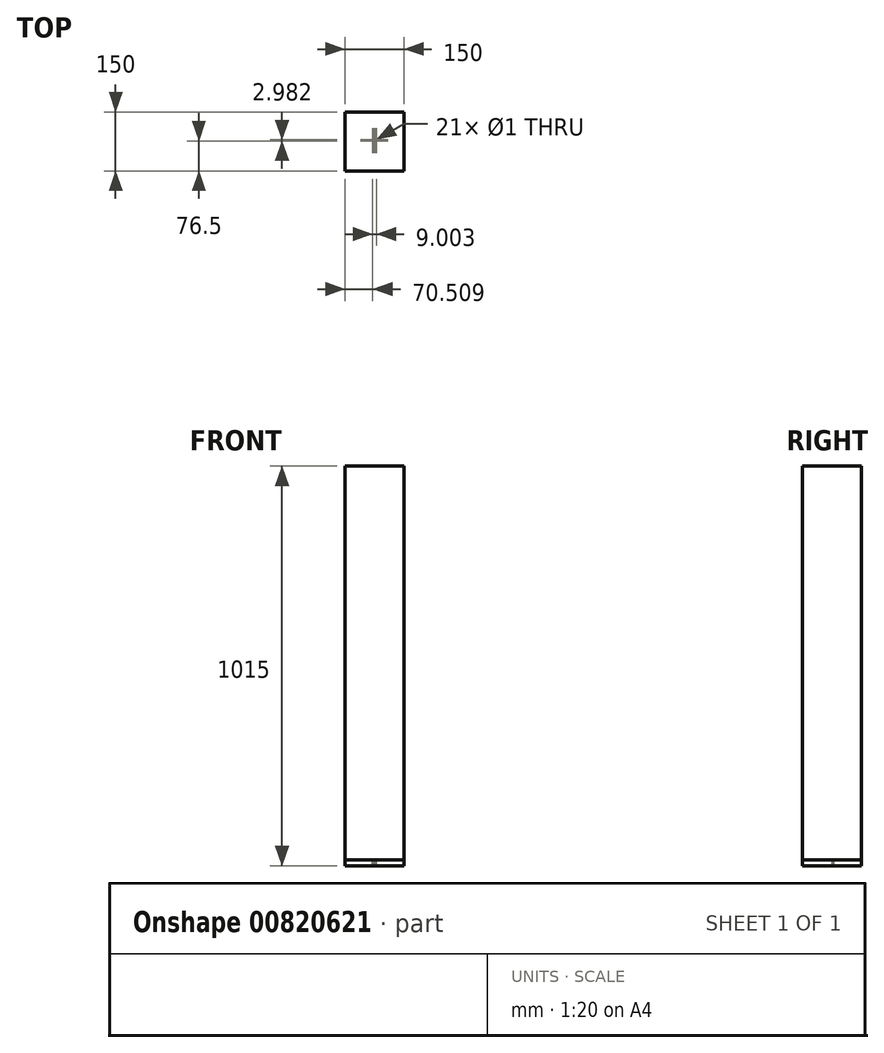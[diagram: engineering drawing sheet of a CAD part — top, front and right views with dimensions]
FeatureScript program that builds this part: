
annotation { "Feature Type Name" : "Feature", "Feature Type Description" : "" }
export const myFeature = defineFeature(function(context is Context, id is Id, definition is map)
    precondition{}
    {
        {
            var Q0;
            Q0=qCreatedBy(makeId("Top.planeOp"),FACE);
            var sketch = newSketch(context, id + "F0", { "sketchPlane" : qUnion([Q0])});
            skLineSegment(sketch, "E0.bottom", {"start": v(75, -75) * mm, "end": v(-75, -75) * mm});
            skLineSegment(sketch, "E0.top", {"start": v(75, 75) * mm, "end": v(-75, 75) * mm});
            skLineSegment(sketch, "E0.left", {"start": v(75, -75) * mm, "end": v(75, 75) * mm});
            skLineSegment(sketch, "E0.right", {"start": v(-75, -75) * mm, "end": v(-75, 75) * mm});
            skPoint(sketch, "E0.middle", {"position": v(0, 0) * mm});
            skSolve(sketch);
        }
        {
            var Q0;
            Q0=makeQuery(id+"F0.imprint","IMPRINT",FACE,{"disambiguationData":[TD([[makeQuery(id+"F0.imprint","IMPRINT",EDGE,{"derivedFrom":sQuery(id+"F0.wireOp",EDGE,"E0.bottom")}),-1.0]])]});
            extrude(context, id + "F1", {"entities" : qUnion([Q0]), "depth" : 1000 * mm, "offsetDistance" : 25 * mm});
        }
        {
            var Q0;
            Q0=makeQuery(id+"F1.opExtrude","CAP_FACE",FACE,{"disambiguationData":[OSD([sQuery(id+"F0.wireOp",EDGE,"E0.bottom"),sQuery(id+"F0.wireOp",EDGE,"E0.top"),sQuery(id+"F0.wireOp",EDGE,"E0.left"),sQuery(id+"F0.wireOp",EDGE,"E0.right")])],"isStart":true});
            var sketch = newSketch(context, id + "F2", { "sketchPlane" : qUnion([Q0])});
            skCircle(sketch, "E1", {"center": v(0, 0) * mm, "radius": 0.5 * mm});
            skCircle(sketch, "E2.1.0.0", {"center": v(1.5, 0) * mm, "radius": 0.5 * mm});
            skCircle(sketch, "E3.0.2.0", {"center": v(3, 0) * mm, "radius": 0.5 * mm});
            skCircle(sketch, "E4.0.3.0", {"center": v(4.5, 0) * mm, "radius": 0.5 * mm});
            skCircle(sketch, "E5.1.0.0", {"center": v(-1.5, 0) * mm, "radius": 0.5 * mm});
            skCircle(sketch, "E5.2.0.0", {"center": v(-3, 0) * mm, "radius": 0.5 * mm});
            skCircle(sketch, "E5.3.0.0", {"center": v(-4.5, 0) * mm, "radius": 0.5 * mm});
            skCircle(sketch, "E6", {"center": v(0.01, 1.5) * mm, "radius": 0.5 * mm});
            skCircle(sketch, "E7.1.0.0", {"center": v(1.51, 1.5) * mm, "radius": 0.5 * mm});
            skCircle(sketch, "E7.2.0.0", {"center": v(3.01, 1.5) * mm, "radius": 0.5 * mm});
            skCircle(sketch, "E7.3.0.0", {"center": v(4.51, 1.5) * mm, "radius": 0.5 * mm});
            skCircle(sketch, "E8.1.0.0", {"center": v(-1.49, 1.5) * mm, "radius": 0.5 * mm});
            skCircle(sketch, "E8.2.0.0", {"center": v(-2.99, 1.5) * mm, "radius": 0.5 * mm});
            skCircle(sketch, "E8.3.0.0", {"center": v(-4.49, 1.5) * mm, "radius": 0.5 * mm});
            skCircle(sketch, "E9", {"center": v(0, 3) * mm, "radius": 0.5 * mm});
            skCircle(sketch, "E10", {"center": v(0, 4.48) * mm, "radius": 0.5 * mm});
            skCircle(sketch, "E11.1.0.0", {"center": v(1.5, 3) * mm, "radius": 0.5 * mm});
            skCircle(sketch, "E11.1.0.1", {"center": v(1.5, 4.48) * mm, "radius": 0.5 * mm});
            skCircle(sketch, "E11.2.0.0", {"center": v(3, 3) * mm, "radius": 0.5 * mm});
            skCircle(sketch, "E11.2.0.1", {"center": v(3, 4.48) * mm, "radius": 0.5 * mm});
            skCircle(sketch, "E11.3.0.0", {"center": v(4.5, 3) * mm, "radius": 0.5 * mm});
            skCircle(sketch, "E11.3.0.1", {"center": v(4.5, 4.48) * mm, "radius": 0.5 * mm});
            skLineSegment(sketch, "E11.direction1", {"start": v(0, 3) * mm, "end": v(1.5, 3) * mm, "construction": true});
            skCircle(sketch, "E12.1.0.0", {"center": v(-1.5, 4.48) * mm, "radius": 0.5 * mm});
            skCircle(sketch, "E12.1.0.1", {"center": v(-1.5, 3) * mm, "radius": 0.5 * mm});
            skCircle(sketch, "E12.2.0.0", {"center": v(-3, 4.48) * mm, "radius": 0.5 * mm});
            skCircle(sketch, "E12.2.0.1", {"center": v(-3, 3) * mm, "radius": 0.5 * mm});
            skCircle(sketch, "E12.3.0.0", {"center": v(-4.5, 4.48) * mm, "radius": 0.5 * mm});
            skCircle(sketch, "E12.3.0.1", {"center": v(-4.5, 3) * mm, "radius": 0.5 * mm});
            skLineSegment(sketch, "E12.direction1", {"start": v(0, 4.48) * mm, "end": v(-1.5, 4.48) * mm, "construction": true});
            skCircle(sketch, "E13.MirrorC", {"center": v(-3, -4.48) * mm, "radius": 0.5 * mm});
            skCircle(sketch, "E14.MirrorC", {"center": v(-2.99, -1.5) * mm, "radius": 0.5 * mm});
            skCircle(sketch, "E15.MirrorC", {"center": v(3, -3) * mm, "radius": 0.5 * mm});
            skCircle(sketch, "E16.MirrorC", {"center": v(1.5, -3) * mm, "radius": 0.5 * mm});
            skCircle(sketch, "E17.MirrorC", {"center": v(3, -4.48) * mm, "radius": 0.5 * mm});
            skCircle(sketch, "E18.MirrorC", {"center": v(0, -4.48) * mm, "radius": 0.5 * mm});
            skCircle(sketch, "E19.MirrorC", {"center": v(-1.5, -4.48) * mm, "radius": 0.5 * mm});
            skCircle(sketch, "E20.MirrorC", {"center": v(4.5, -4.48) * mm, "radius": 0.5 * mm});
            skCircle(sketch, "E21.MirrorC", {"center": v(0, -3) * mm, "radius": 0.5 * mm});
            skCircle(sketch, "E22.MirrorC", {"center": v(-3, -3) * mm, "radius": 0.5 * mm});
            skCircle(sketch, "E23.MirrorC", {"center": v(-1.49, -1.5) * mm, "radius": 0.5 * mm});
            skCircle(sketch, "E24.MirrorC", {"center": v(-4.5, -3) * mm, "radius": 0.5 * mm});
            skCircle(sketch, "E25.MirrorC", {"center": v(-1.5, -3) * mm, "radius": 0.5 * mm});
            skCircle(sketch, "E26.MirrorC", {"center": v(-4.49, -1.5) * mm, "radius": 0.5 * mm});
            skLineSegment(sketch, "E27.MirrorCS", {"start": v(0, -3) * mm, "end": v(1.5, -3) * mm, "construction": true});
            skLineSegment(sketch, "E28.MirrorCS", {"start": v(0, -4.48) * mm, "end": v(-1.5, -4.48) * mm, "construction": true});
            skCircle(sketch, "E29.MirrorC", {"center": v(-4.5, -4.48) * mm, "radius": 0.5 * mm});
            skCircle(sketch, "E30.MirrorC", {"center": v(1.51, -1.5) * mm, "radius": 0.5 * mm});
            skCircle(sketch, "E31.MirrorC", {"center": v(1.5, -4.48) * mm, "radius": 0.5 * mm});
            skCircle(sketch, "E32.MirrorC", {"center": v(0.01, -1.5) * mm, "radius": 0.5 * mm});
            skCircle(sketch, "E33.MirrorC", {"center": v(3.01, -1.5) * mm, "radius": 0.5 * mm});
            skCircle(sketch, "E34.MirrorC", {"center": v(4.5, -3) * mm, "radius": 0.5 * mm});
            skCircle(sketch, "E35.MirrorC", {"center": v(4.51, -1.5) * mm, "radius": 0.5 * mm});
            skSolve(sketch);
        }
        {
            var Q0;
            Q0=makeQuery(id+"F2.imprint","IMPRINT",FACE,{"disambiguationData":[TD([[makeQuery(id+"F2.imprint","IMPRINT",EDGE,{"derivedFrom":sQuery(id+"F2.wireOp",EDGE,"E15.MirrorC")}),-1.0]])]});
            var Q1;
            Q1=makeQuery(id+"F2.imprint","IMPRINT",FACE,{"disambiguationData":[TD([[makeQuery(id+"F2.imprint","IMPRINT",EDGE,{"derivedFrom":sQuery(id+"F2.wireOp",EDGE,"E12.2.0.0")}),1.0]])]});
            var Q2;
            Q2=makeQuery(id+"F2.imprint","IMPRINT",FACE,{"disambiguationData":[TD([[makeQuery(id+"F2.imprint","IMPRINT",EDGE,{"derivedFrom":sQuery(id+"F2.wireOp",EDGE,"E30.MirrorC")}),-1.0]])]});
            var Q3;
            Q3=makeQuery(id+"F2.imprint","IMPRINT",FACE,{"disambiguationData":[TD([[makeQuery(id+"F2.imprint","IMPRINT",EDGE,{"derivedFrom":sQuery(id+"F2.wireOp",EDGE,"E22.MirrorC")}),-1.0]])]});
            var Q4;
            Q4=makeQuery(id+"F2.imprint","IMPRINT",FACE,{"disambiguationData":[TD([[makeQuery(id+"F2.imprint","IMPRINT",EDGE,{"derivedFrom":sQuery(id+"F2.wireOp",EDGE,"E8.3.0.0")}),1.0]])]});
            var Q5;
            Q5=makeQuery(id+"F2.imprint","IMPRINT",FACE,{"disambiguationData":[TD([[makeQuery(id+"F2.imprint","IMPRINT",EDGE,{"derivedFrom":sQuery(id+"F2.wireOp",EDGE,"E11.3.0.1")}),1.0]])]});
            var Q6;
            Q6=makeQuery(id+"F2.imprint","IMPRINT",FACE,{"disambiguationData":[TD([[makeQuery(id+"F2.imprint","IMPRINT",EDGE,{"derivedFrom":sQuery(id+"F2.wireOp",EDGE,"E12.3.0.1")}),1.0]])]});
            var Q7;
            Q7=makeQuery(id+"F2.imprint","IMPRINT",FACE,{"disambiguationData":[TD([[makeQuery(id+"F2.imprint","IMPRINT",EDGE,{"derivedFrom":sQuery(id+"F2.wireOp",EDGE,"E11.1.0.1")}),1.0]])]});
            var Q8;
            Q8=makeQuery(id+"F2.imprint","IMPRINT",FACE,{"disambiguationData":[TD([[makeQuery(id+"F2.imprint","IMPRINT",EDGE,{"derivedFrom":sQuery(id+"F2.wireOp",EDGE,"E11.2.0.0")}),1.0]])]});
            var Q9;
            Q9=makeQuery(id+"F2.imprint","IMPRINT",FACE,{"disambiguationData":[TD([[makeQuery(id+"F2.imprint","IMPRINT",EDGE,{"derivedFrom":sQuery(id+"F2.wireOp",EDGE,"E24.MirrorC")}),-1.0]])]});
            var Q10;
            Q10=makeQuery(id+"F2.imprint","IMPRINT",FACE,{"disambiguationData":[TD([[makeQuery(id+"F2.imprint","IMPRINT",EDGE,{"derivedFrom":sQuery(id+"F2.wireOp",EDGE,"E12.1.0.1")}),1.0]])]});
            var Q11;
            Q11=makeQuery(id+"F2.imprint","IMPRINT",FACE,{"disambiguationData":[TD([[makeQuery(id+"F2.imprint","IMPRINT",EDGE,{"derivedFrom":sQuery(id+"F2.wireOp",EDGE,"E25.MirrorC")}),-1.0]])]});
            var Q12;
            Q12=makeQuery(id+"F2.imprint","IMPRINT",FACE,{"disambiguationData":[TD([[makeQuery(id+"F2.imprint","IMPRINT",EDGE,{"derivedFrom":sQuery(id+"F2.wireOp",EDGE,"E33.MirrorC")}),-1.0]])]});
            var Q13;
            Q13=makeQuery(id+"F2.imprint","IMPRINT",FACE,{"disambiguationData":[TD([[makeQuery(id+"F2.imprint","IMPRINT",EDGE,{"derivedFrom":sQuery(id+"F2.wireOp",EDGE,"E13.MirrorC")}),-1.0]])]});
            var Q14;
            Q14=makeQuery(id+"F2.imprint","IMPRINT",FACE,{"disambiguationData":[TD([[makeQuery(id+"F2.imprint","IMPRINT",EDGE,{"derivedFrom":sQuery(id+"F2.wireOp",EDGE,"E31.MirrorC")}),-1.0]])]});
            var Q15;
            Q15=makeQuery(id+"F2.imprint","IMPRINT",FACE,{"disambiguationData":[TD([[makeQuery(id+"F2.imprint","IMPRINT",EDGE,{"derivedFrom":sQuery(id+"F2.wireOp",EDGE,"E1")}),1.0]])]});
            var Q16;
            Q16=makeQuery(id+"F2.imprint","IMPRINT",FACE,{"disambiguationData":[TD([[makeQuery(id+"F2.imprint","IMPRINT",EDGE,{"derivedFrom":sQuery(id+"F2.wireOp",EDGE,"E2.1.0.0")}),1.0]])]});
            var Q17;
            Q17=makeQuery(id+"F2.imprint","IMPRINT",FACE,{"disambiguationData":[TD([[makeQuery(id+"F2.imprint","IMPRINT",EDGE,{"derivedFrom":sQuery(id+"F2.wireOp",EDGE,"E3.0.2.0")}),1.0]])]});
            var Q18;
            Q18=makeQuery(id+"F2.imprint","IMPRINT",FACE,{"disambiguationData":[TD([[makeQuery(id+"F2.imprint","IMPRINT",EDGE,{"derivedFrom":sQuery(id+"F2.wireOp",EDGE,"E4.0.3.0")}),1.0]])]});
            var Q19;
            Q19=makeQuery(id+"F2.imprint","IMPRINT",FACE,{"disambiguationData":[TD([[makeQuery(id+"F2.imprint","IMPRINT",EDGE,{"derivedFrom":sQuery(id+"F2.wireOp",EDGE,"E5.1.0.0")}),1.0]])]});
            var Q20;
            Q20=makeQuery(id+"F2.imprint","IMPRINT",FACE,{"disambiguationData":[TD([[makeQuery(id+"F2.imprint","IMPRINT",EDGE,{"derivedFrom":sQuery(id+"F2.wireOp",EDGE,"E5.2.0.0")}),1.0]])]});
            var Q21;
            Q21=makeQuery(id+"F2.imprint","IMPRINT",FACE,{"disambiguationData":[TD([[makeQuery(id+"F2.imprint","IMPRINT",EDGE,{"derivedFrom":sQuery(id+"F2.wireOp",EDGE,"E5.3.0.0")}),1.0]])]});
            var Q22;
            Q22=makeQuery(id+"F2.imprint","IMPRINT",FACE,{"disambiguationData":[TD([[makeQuery(id+"F2.imprint","IMPRINT",EDGE,{"derivedFrom":sQuery(id+"F2.wireOp",EDGE,"E6")}),1.0]])]});
            var Q23;
            Q23=makeQuery(id+"F2.imprint","IMPRINT",FACE,{"disambiguationData":[TD([[makeQuery(id+"F2.imprint","IMPRINT",EDGE,{"derivedFrom":sQuery(id+"F2.wireOp",EDGE,"E7.1.0.0")}),1.0]])]});
            var Q24;
            Q24=makeQuery(id+"F2.imprint","IMPRINT",FACE,{"disambiguationData":[TD([[makeQuery(id+"F2.imprint","IMPRINT",EDGE,{"derivedFrom":sQuery(id+"F2.wireOp",EDGE,"E7.2.0.0")}),1.0]])]});
            var Q25;
            Q25=makeQuery(id+"F2.imprint","IMPRINT",FACE,{"disambiguationData":[TD([[makeQuery(id+"F2.imprint","IMPRINT",EDGE,{"derivedFrom":sQuery(id+"F2.wireOp",EDGE,"E7.3.0.0")}),1.0]])]});
            var Q26;
            Q26=makeQuery(id+"F2.imprint","IMPRINT",FACE,{"disambiguationData":[TD([[makeQuery(id+"F2.imprint","IMPRINT",EDGE,{"derivedFrom":sQuery(id+"F2.wireOp",EDGE,"E34.MirrorC")}),-1.0]])]});
            var Q27;
            Q27=makeQuery(id+"F2.imprint","IMPRINT",FACE,{"disambiguationData":[TD([[makeQuery(id+"F2.imprint","IMPRINT",EDGE,{"derivedFrom":sQuery(id+"F2.wireOp",EDGE,"E8.1.0.0")}),1.0]])]});
            var Q28;
            Q28=makeQuery(id+"F2.imprint","IMPRINT",FACE,{"disambiguationData":[TD([[makeQuery(id+"F2.imprint","IMPRINT",EDGE,{"derivedFrom":sQuery(id+"F2.wireOp",EDGE,"E26.MirrorC")}),-1.0]])]});
            var Q29;
            Q29=makeQuery(id+"F2.imprint","IMPRINT",FACE,{"disambiguationData":[TD([[makeQuery(id+"F2.imprint","IMPRINT",EDGE,{"derivedFrom":sQuery(id+"F2.wireOp",EDGE,"E12.2.0.1")}),1.0]])]});
            var Q30;
            Q30=makeQuery(id+"F2.imprint","IMPRINT",FACE,{"disambiguationData":[TD([[makeQuery(id+"F2.imprint","IMPRINT",EDGE,{"derivedFrom":sQuery(id+"F2.wireOp",EDGE,"E8.2.0.0")}),1.0]])]});
            var Q31;
            Q31=makeQuery(id+"F2.imprint","IMPRINT",FACE,{"disambiguationData":[TD([[makeQuery(id+"F2.imprint","IMPRINT",EDGE,{"derivedFrom":sQuery(id+"F2.wireOp",EDGE,"E20.MirrorC")}),-1.0]])]});
            var Q32;
            Q32=makeQuery(id+"F2.imprint","IMPRINT",FACE,{"disambiguationData":[TD([[makeQuery(id+"F2.imprint","IMPRINT",EDGE,{"derivedFrom":sQuery(id+"F2.wireOp",EDGE,"E11.2.0.1")}),1.0]])]});
            var Q33;
            Q33=makeQuery(id+"F2.imprint","IMPRINT",FACE,{"disambiguationData":[TD([[makeQuery(id+"F2.imprint","IMPRINT",EDGE,{"derivedFrom":sQuery(id+"F2.wireOp",EDGE,"E23.MirrorC")}),-1.0]])]});
            var Q34;
            Q34=makeQuery(id+"F2.imprint","IMPRINT",FACE,{"disambiguationData":[TD([[makeQuery(id+"F2.imprint","IMPRINT",EDGE,{"derivedFrom":sQuery(id+"F2.wireOp",EDGE,"E29.MirrorC")}),-1.0]])]});
            var Q35;
            Q35=makeQuery(id+"F2.imprint","IMPRINT",FACE,{"disambiguationData":[TD([[makeQuery(id+"F2.imprint","IMPRINT",EDGE,{"derivedFrom":sQuery(id+"F2.wireOp",EDGE,"E12.3.0.0")}),1.0]])]});
            var Q36;
            Q36=makeQuery(id+"F2.imprint","IMPRINT",FACE,{"disambiguationData":[TD([[makeQuery(id+"F2.imprint","IMPRINT",EDGE,{"derivedFrom":sQuery(id+"F2.wireOp",EDGE,"E35.MirrorC")}),-1.0]])]});
            var Q37;
            Q37=makeQuery(id+"F2.imprint","IMPRINT",FACE,{"disambiguationData":[TD([[makeQuery(id+"F2.imprint","IMPRINT",EDGE,{"derivedFrom":sQuery(id+"F2.wireOp",EDGE,"E14.MirrorC")}),-1.0]])]});
            var Q38;
            Q38=makeQuery(id+"F2.imprint","IMPRINT",FACE,{"disambiguationData":[TD([[makeQuery(id+"F2.imprint","IMPRINT",EDGE,{"derivedFrom":sQuery(id+"F2.wireOp",EDGE,"E11.3.0.0")}),1.0]])]});
            var Q39;
            Q39=makeQuery(id+"F2.imprint","IMPRINT",FACE,{"disambiguationData":[TD([[makeQuery(id+"F2.imprint","IMPRINT",EDGE,{"derivedFrom":sQuery(id+"F2.wireOp",EDGE,"E32.MirrorC")}),-1.0]])]});
            var Q40;
            Q40=makeQuery(id+"F2.imprint","IMPRINT",FACE,{"disambiguationData":[TD([[makeQuery(id+"F2.imprint","IMPRINT",EDGE,{"derivedFrom":sQuery(id+"F2.wireOp",EDGE,"E17.MirrorC")}),-1.0]])]});
            var Q41;
            Q41=makeQuery(id+"F2.imprint","IMPRINT",FACE,{"disambiguationData":[TD([[makeQuery(id+"F2.imprint","IMPRINT",EDGE,{"derivedFrom":sQuery(id+"F2.wireOp",EDGE,"E18.MirrorC")}),-1.0]])]});
            var Q42;
            Q42=makeQuery(id+"F2.imprint","IMPRINT",FACE,{"disambiguationData":[TD([[makeQuery(id+"F2.imprint","IMPRINT",EDGE,{"derivedFrom":sQuery(id+"F2.wireOp",EDGE,"E19.MirrorC")}),-1.0]])]});
            var Q43;
            Q43=makeQuery(id+"F2.imprint","IMPRINT",FACE,{"disambiguationData":[TD([[makeQuery(id+"F2.imprint","IMPRINT",EDGE,{"derivedFrom":sQuery(id+"F2.wireOp",EDGE,"E10")}),1.0]])]});
            var Q44;
            Q44=makeQuery(id+"F2.imprint","IMPRINT",FACE,{"disambiguationData":[TD([[makeQuery(id+"F2.imprint","IMPRINT",EDGE,{"derivedFrom":sQuery(id+"F2.wireOp",EDGE,"E12.1.0.0")}),1.0]])]});
            var Q45;
            Q45=makeQuery(id+"F2.imprint","IMPRINT",FACE,{"disambiguationData":[TD([[makeQuery(id+"F2.imprint","IMPRINT",EDGE,{"derivedFrom":sQuery(id+"F2.wireOp",EDGE,"E16.MirrorC")}),-1.0]])]});
            var Q46;
            Q46=makeQuery(id+"F2.imprint","IMPRINT",FACE,{"disambiguationData":[TD([[makeQuery(id+"F2.imprint","IMPRINT",EDGE,{"derivedFrom":sQuery(id+"F2.wireOp",EDGE,"E21.MirrorC")}),-1.0]])]});
            var Q47;
            Q47=makeQuery(id+"F2.imprint","IMPRINT",FACE,{"disambiguationData":[TD([[makeQuery(id+"F2.imprint","IMPRINT",EDGE,{"derivedFrom":sQuery(id+"F2.wireOp",EDGE,"E9")}),1.0]])]});
            var Q48;
            Q48=makeQuery(id+"F2.imprint","IMPRINT",FACE,{"disambiguationData":[TD([[makeQuery(id+"F2.imprint","IMPRINT",EDGE,{"derivedFrom":sQuery(id+"F2.wireOp",EDGE,"E11.1.0.0")}),1.0]])]});
            extrude(context, id + "F3", {"entities" : qUnion([Q0, Q1, Q2, Q3, Q4, Q5, Q6, Q7, Q8, Q9, Q10, Q11, Q12, Q13, Q14, Q15, Q16, Q17, Q18, Q19, Q20, Q21, Q22, Q23, Q24, Q25, Q26, Q27, Q28, Q29, Q30, Q31, Q32, Q33, Q34, Q35, Q36, Q37, Q38, Q39, Q40, Q41, Q42, Q43, Q44, Q45, Q46, Q47, Q48]), "depth" : 15 * mm, "offsetDistance" : 25 * mm});
        }
    });
